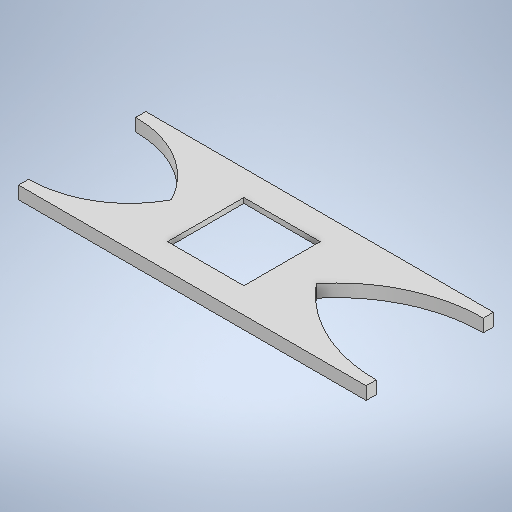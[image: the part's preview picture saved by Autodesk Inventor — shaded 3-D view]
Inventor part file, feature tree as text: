
AUTODESK INVENTOR PART (.ipt)
format: ipt  version: 2025 (Build 290162000, 162)  size: 288,256 bytes
history: native  units: mm
features: extrude x3, sketch x3
ambient origin geometry x8: Origin, YZ Plane, XZ Plane, XY Plane, X Axis, Y Axis, Z Axis, Center Point
bodies: Solid1 (feature_tree)
feature tree (6):
  extrude  "Extrusion1"  Depth=50.0mm
  extrude  "Extrusion2"  Depth=5.0mm
  extrude  "Extrusion3"  Depth=40.0mm
  sketch  "Sketch1"  dims[d0=136.525mm d1=50.0mm]
  sketch  "Sketch2"  dims[d2=5.0mm d3=0.0mm d4=51.0mm]
  sketch  "Sketch3"  dims[d5=63.5mm d6=40.0mm d7=20.0mm d8=3.0mm d9=0.0mm d10=4.0mm d11=4.0mm d12=3.0mm d13=4.0mm d14=4.0mm d15=3.0mm d16=30.0mm d17=30.0mm d18=3.0mm d19=0.0mm]
